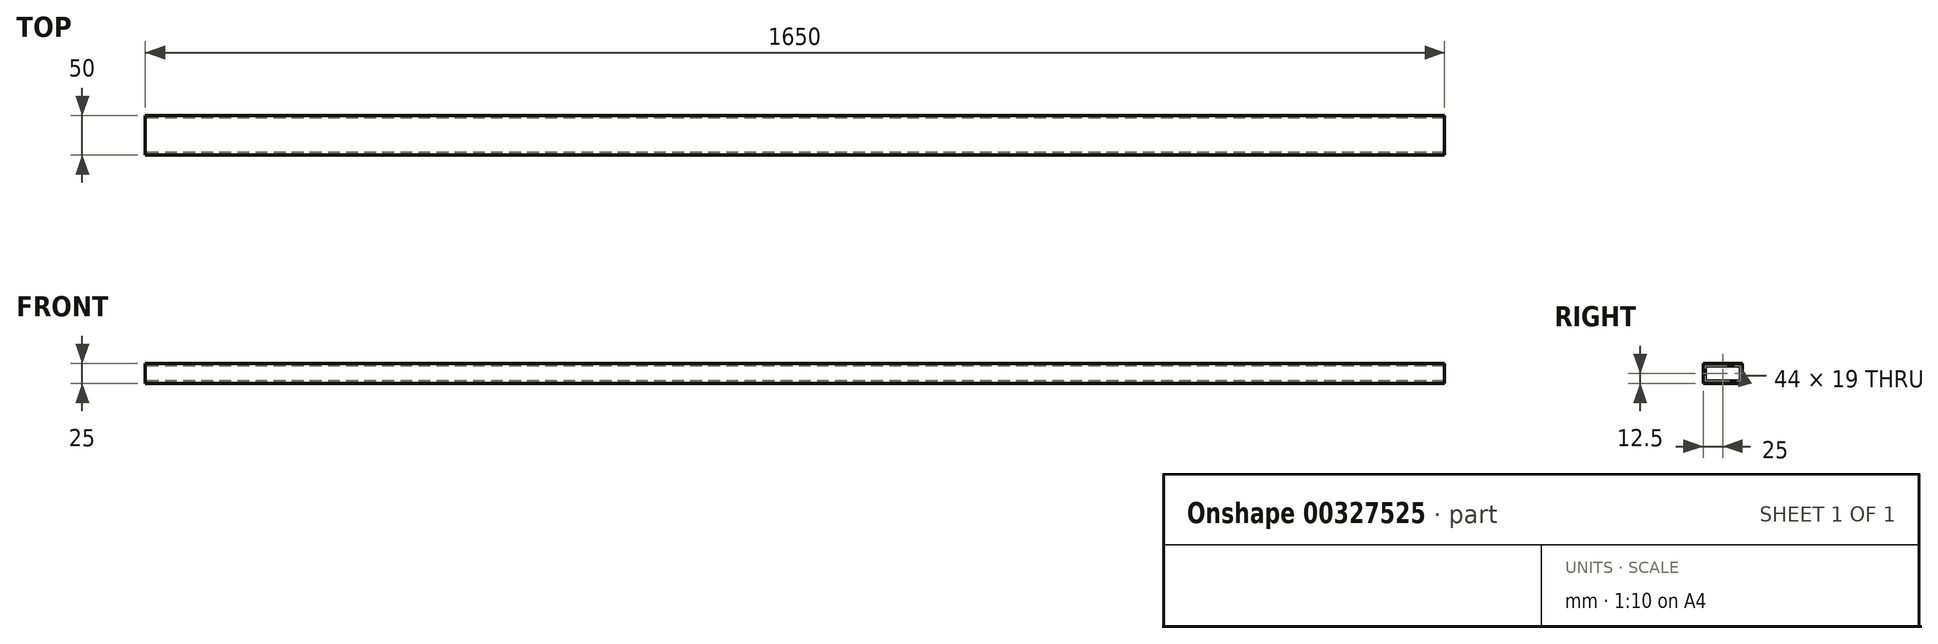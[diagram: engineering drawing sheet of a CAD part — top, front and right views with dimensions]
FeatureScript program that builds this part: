
annotation { "Feature Type Name" : "Feature", "Feature Type Description" : "" }
export const myFeature = defineFeature(function(context is Context, id is Id, definition is map)
    precondition{}
    {
        {
            var Q0;
            Q0=qCreatedBy(makeId("Right.planeOp"),FACE);
            var sketch = newSketch(context, id + "F0", { "sketchPlane" : qUnion([Q0])});
            skLineSegment(sketch, "E0.bottom", {"start": v(-25, 12.5) * mm, "end": v(25, 12.5) * mm});
            skLineSegment(sketch, "E0.top", {"start": v(-25, -12.5) * mm, "end": v(25, -12.5) * mm});
            skLineSegment(sketch, "E0.left", {"start": v(-25, 12.5) * mm, "end": v(-25, -12.5) * mm});
            skLineSegment(sketch, "E0.right", {"start": v(25, 12.5) * mm, "end": v(25, -12.5) * mm});
            skPoint(sketch, "E0.middle", {"position": v(0, 0) * mm});
            skLineSegment(sketch, "E1.bottom", {"start": v(-22, 9.5) * mm, "end": v(22, 9.5) * mm});
            skLineSegment(sketch, "E1.top", {"start": v(-22, -9.5) * mm, "end": v(22, -9.5) * mm});
            skLineSegment(sketch, "E1.left", {"start": v(-22, 9.5) * mm, "end": v(-22, -9.5) * mm});
            skLineSegment(sketch, "E1.right", {"start": v(22, 9.5) * mm, "end": v(22, -9.5) * mm});
            skSolve(sketch);
        }
        {
            var Q0;
            Q0=makeQuery(id+"F0.imprint","IMPRINT",FACE,{"disambiguationData":[TD([[makeQuery(id+"F0.imprint","IMPRINT",EDGE,{"derivedFrom":sQuery(id+"F0.wireOp",EDGE,"E0.bottom")}),-1.0]])]});
            extrude(context, id + "F1", {"entities" : qUnion([Q0]), "depth" : 1650 * mm, "symmetric" : true});
        }
    });
